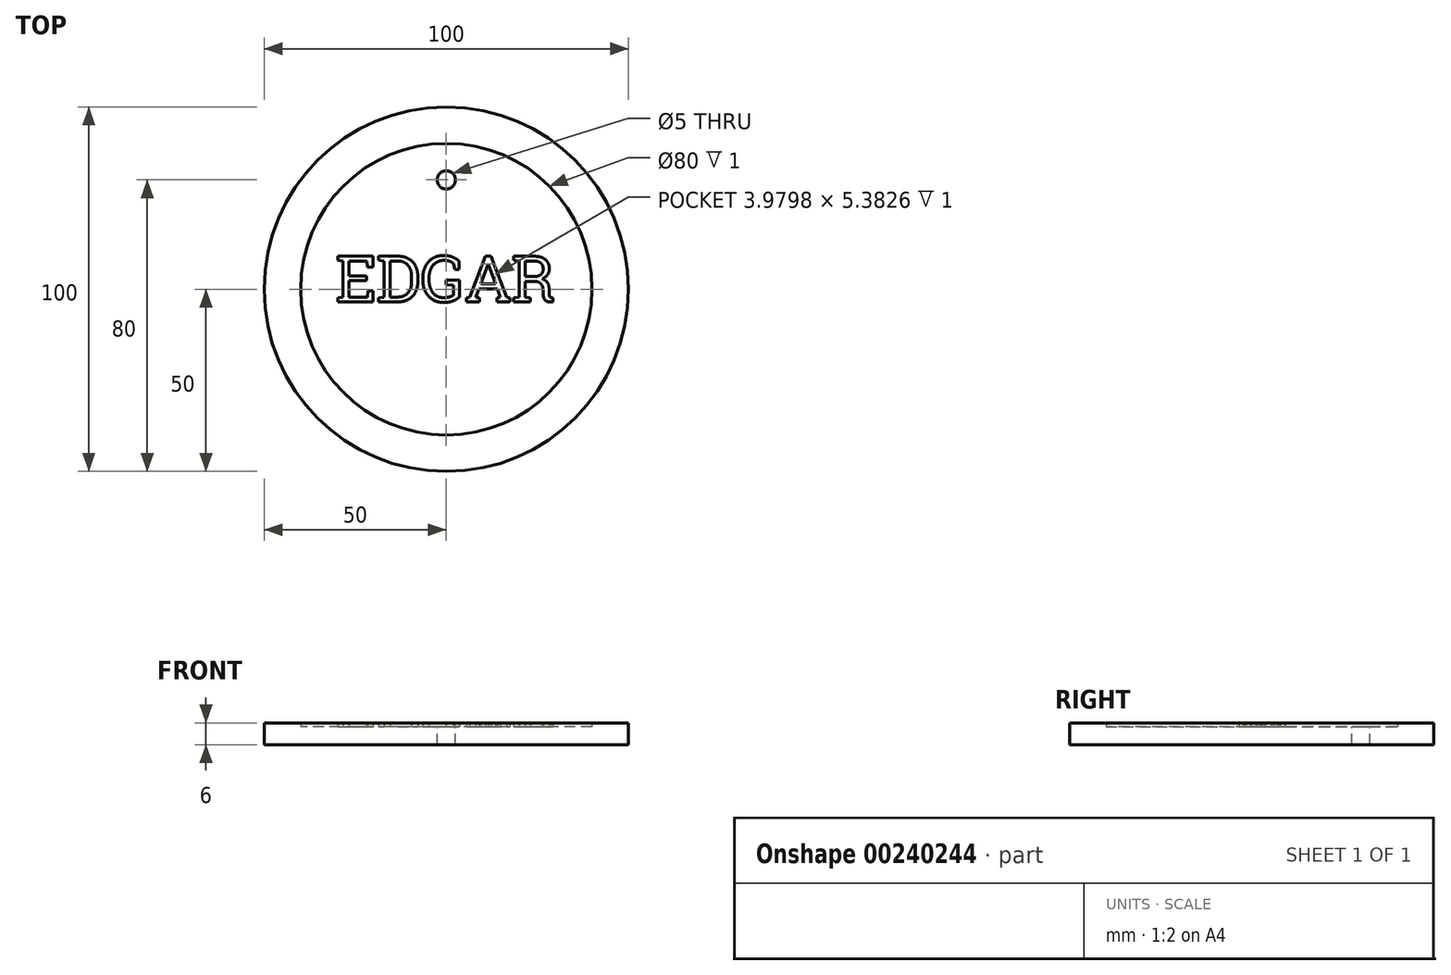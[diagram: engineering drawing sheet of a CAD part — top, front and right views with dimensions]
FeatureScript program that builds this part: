
annotation { "Feature Type Name" : "Feature", "Feature Type Description" : "" }
export const myFeature = defineFeature(function(context is Context, id is Id, definition is map)
    precondition{}
    {
        {
            var Q0;
            Q0=qCreatedBy(makeId("Top.planeOp"),FACE);
            var sketch = newSketch(context, id + "F0", { "sketchPlane" : qUnion([Q0])});
            skCircle(sketch, "E0", {"center": v(0, 0) * mm, "radius": 50 * mm});
            skSolve(sketch);
        }
        {
            var Q0;
            Q0=makeQuery(id+"F0.imprint","IMPRINT",FACE,{"disambiguationData":[TD([[makeQuery(id+"F0.imprint","IMPRINT",EDGE,{"derivedFrom":sQuery(id+"F0.wireOp",EDGE,"E0")}),1.0]])]});
            extrude(context, id + "F1", {"entities" : qUnion([Q0]), "depth" : 5 * mm});
        }
        {
            var Q0;
            Q0=makeQuery(id+"F1.opExtrude","CAP_FACE",FACE,{"disambiguationData":[OSD([sQuery(id+"F0.wireOp",EDGE,"E0")])],"isStart":false});
            var sketch = newSketch(context, id + "F2", { "sketchPlane" : qUnion([Q0])});
            skLineSegment(sketch, "E1", {"start": v(0, 0) * mm, "end": v(0, 30) * mm, "construction": true});
            skCircle(sketch, "E2", {"center": v(0, 30) * mm, "radius": 2.5 * mm});
            skSolve(sketch);
        }
        {
            var Q0;
            Q0=makeQuery(id+"F2.imprint","IMPRINT",FACE,{"disambiguationData":[TD([[makeQuery(id+"F2.imprint","IMPRINT",EDGE,{"derivedFrom":sQuery(id+"F2.wireOp",EDGE,"E2")}),1.0]])]});
            extrude(context, id + "F3", {"entities" : qUnion([Q0]), "operationType" : NewBodyOperationType.REMOVE, "oppositeDirection" : true, "depth" : 5 * mm});
        }
        {
            var Q0;
            Q0=makeQuery(id+"F1.opExtrude","CAP_FACE",FACE,{"disambiguationData":[OSD([sQuery(id+"F0.wireOp",EDGE,"E0")])],"isStart":false});
            var sketch = newSketch(context, id + "F4", { "sketchPlane" : qUnion([Q0])});
            skText(sketch, "E3", { "text": "EDGAR", "fontName": "RobotoSlab-Regular.ttf"});
            const initialGuessF4  = {"E3": [-0.0304, -0.00347, 1, 0, 0.0127]};
            skSetInitialGuess(sketch, initialGuessF4);
            skSolve(sketch);
        }
        {
            var Q0;
            Q0 = qSketchRegion(id + "F4", true);
            extrude(context, id + "F5", {"entities" : qUnion([Q0]), "operationType" : NewBodyOperationType.ADD, "depth" : 1 * mm});
        }
        {
            var Q0;
            {var subQ0=sQuery(id+"F0.wireOp",EDGE,"E0");Q0=makeQuery(id+"F5.boolean.opBoolean","SPLIT",FACE,{"disambiguationData":[TD([makeQuery(id+"F1.opExtrude","SWEPT_FACE",FACE,{"disambiguationData":[OSD([subQ0])]})])],"derivedFrom":makeQuery(id+"F1.opExtrude","CAP_FACE",FACE,{"disambiguationData":[OSD([subQ0])],"isStart":false})});}
            var sketch = newSketch(context, id + "F6", { "sketchPlane" : qUnion([Q0])});
            skCircle(sketch, "E4", {"center": v(0, 0) * mm, "radius": 50 * mm});
            skCircle(sketch, "E5.0", {"center": v(0, 0) * mm, "radius": 40 * mm});
            skSolve(sketch);
        }
        {
            var Q0;
            Q0=makeQuery(id+"F6.imprint","IMPRINT",FACE,{"disambiguationData":[TD([[makeQuery(id+"F6.imprint","IMPRINT",EDGE,{"derivedFrom":sQuery(id+"F6.wireOp",EDGE,"E4")}),1.0]])]});
            extrude(context, id + "F7", {"entities" : qUnion([Q0]), "operationType" : NewBodyOperationType.ADD, "depth" : 1 * mm});
        }
    });
